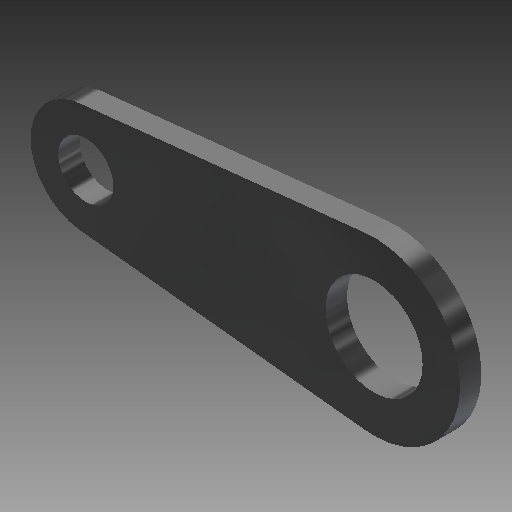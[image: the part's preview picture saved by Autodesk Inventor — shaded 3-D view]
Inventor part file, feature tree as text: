
AUTODESK INVENTOR PART (.ipt)
format: ipt  version: 2019 (Build 230136000, 136)  size: 114,176 bytes
history: native  units: mm
features: sketch x3, hole x2, extrude x1
ambient origin geometry x8: Origin, YZ Plane, XZ Plane, XY Plane, X Axis, Y Axis, Z Axis, Center Point
bodies: Solid1 (feature_tree)
feature tree (6):
  extrude  "Extrusion1"  Depth=28.0mm
  hole  "Hole1"  [1 undecoded]
  hole  "Hole2"  [1 undecoded]
  sketch  "Sketch1"  dims[d0=18.0mm d1=28.0mm]
  sketch  "Sketch2"  dims[d2=47.0mm d3=3.5mm d4=0.0mm]
  sketch  "Sketch3"  dims[d5=15.84mm d6=6.0mm d7=4.0mm d8=2.0mm d9=90.0deg d10=8.0mm d11=20.594885mm d12=9.0mm d13=6.0mm d14=4.0mm d15=2.0mm d16=90.0deg d17=8.0mm d18=20.594885mm]
note: 2 required parameter values undecoded (feature->parameter linkage not recoverable at this tier; creation-order binding heuristic only, values carry confidence <= 0.55)
